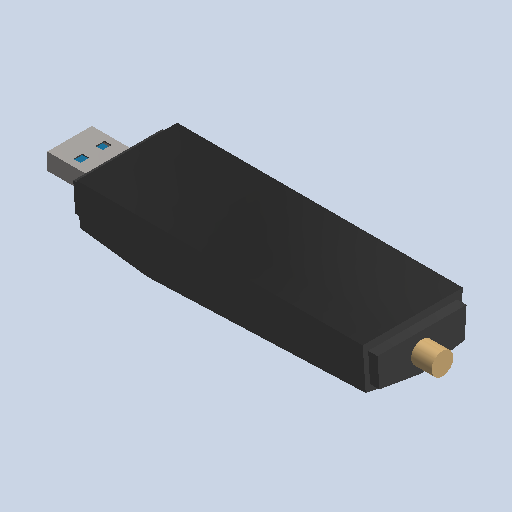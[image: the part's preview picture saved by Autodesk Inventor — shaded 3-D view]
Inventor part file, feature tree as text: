
AUTODESK INVENTOR PART (.ipt)
format: ipt  version: 2022 (Build 260153000, 153)  size: 91,648 bytes
history: mixed  units: mm (DEFAULTED — no unit token found)
features: other x10, chamfer x1, imported_body x1
bodies: Body1 (imported_parasolid), Body2 (imported_parasolid)
feature tree (12):
  other  "Sólido1"
  other  "Origen"
  other  "Plano YZ"
  other  "Plano XZ"
  other  "Plano XY"
  other  "Eje X"
  other  "Eje Y"
  other  "Eje Z"
  other  "Sólido2"
  other  "Boss-Extrude3"
  chamfer  "Chamfer6"  [1 undecoded]
  imported_body  NMx_Import_Brep_tag  [imported B-rep: ~48 faces, bbox_mm=[100.5, 14.0, 27.0]]
note: 1 required parameter value undecoded (feature->parameter linkage not recoverable at this tier; creation-order binding heuristic only, values carry confidence <= 0.55)
